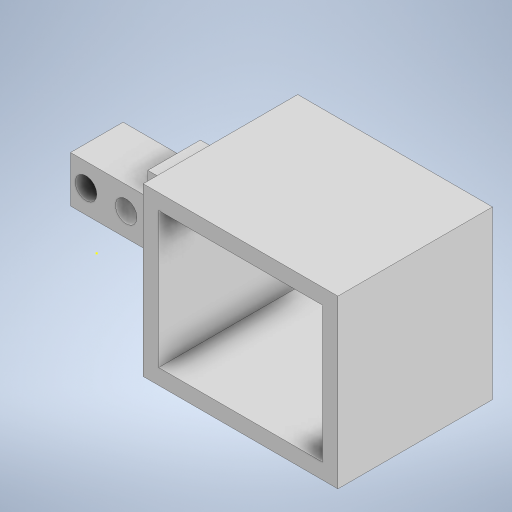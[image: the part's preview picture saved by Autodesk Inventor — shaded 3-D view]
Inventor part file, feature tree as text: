
AUTODESK INVENTOR PART (.ipt)
format: ipt  version: 2024 (Build 280153000, 153)  size: 253,952 bytes
history: native  units: in
note: dims shown in document units (in); Inventor stores cm internally (conversion verified against a paired STEP export)
features: sketch x8, extrude x6
ambient origin geometry x8: Origin, YZ Plane, XZ Plane, XY Plane, X Axis, Y Axis, Z Axis, Center Point
bodies: Solid1 (feature_tree)
feature tree (14):
  extrude  "Extrusion1"  Depth=0.6693in
  extrude  "Extrusion2"  Depth=0.6693in
  extrude  "Extrusion3"  Depth=0.9843in TaperAngle=0.0deg
  extrude  "Extrusion4"  Depth=2.126in
  extrude  "Extrusion5"  Depth=1.9685in
  sketch  "Sketch6"  dims[d13=0.1969in d14=1.9685in]
  extrude  "Extrusion6"  Depth=1.9685in
  sketch  "Sketch8"  dims[d16=2.2835in d17=0.0in d18=0.1969in d19=1.7717in d20=0.0in d21=0.1969in d22=0.2756in d23=0.2756in d24=0.2756in d25=0.0in d26=0.0in]
  sketch  "Sketch1"  dims[d0=1.1811in d1=0.6693in]
  sketch  "Sketch2"  dims[d2=0.5906in d3=0.0in d4=0.6693in]
  sketch  "Sketch3"  dims[d5=0.5906in d6=0.9843in d7=0.0in]
  sketch  "Sketch4"  dims[d8=1.9685in d9=2.126in]
  sketch  "Sketch5"  dims[d10=0.1969in d11=0.0in d12=1.9685in]
  sketch  "Sketch7"  dims[d15=0.1969in]
